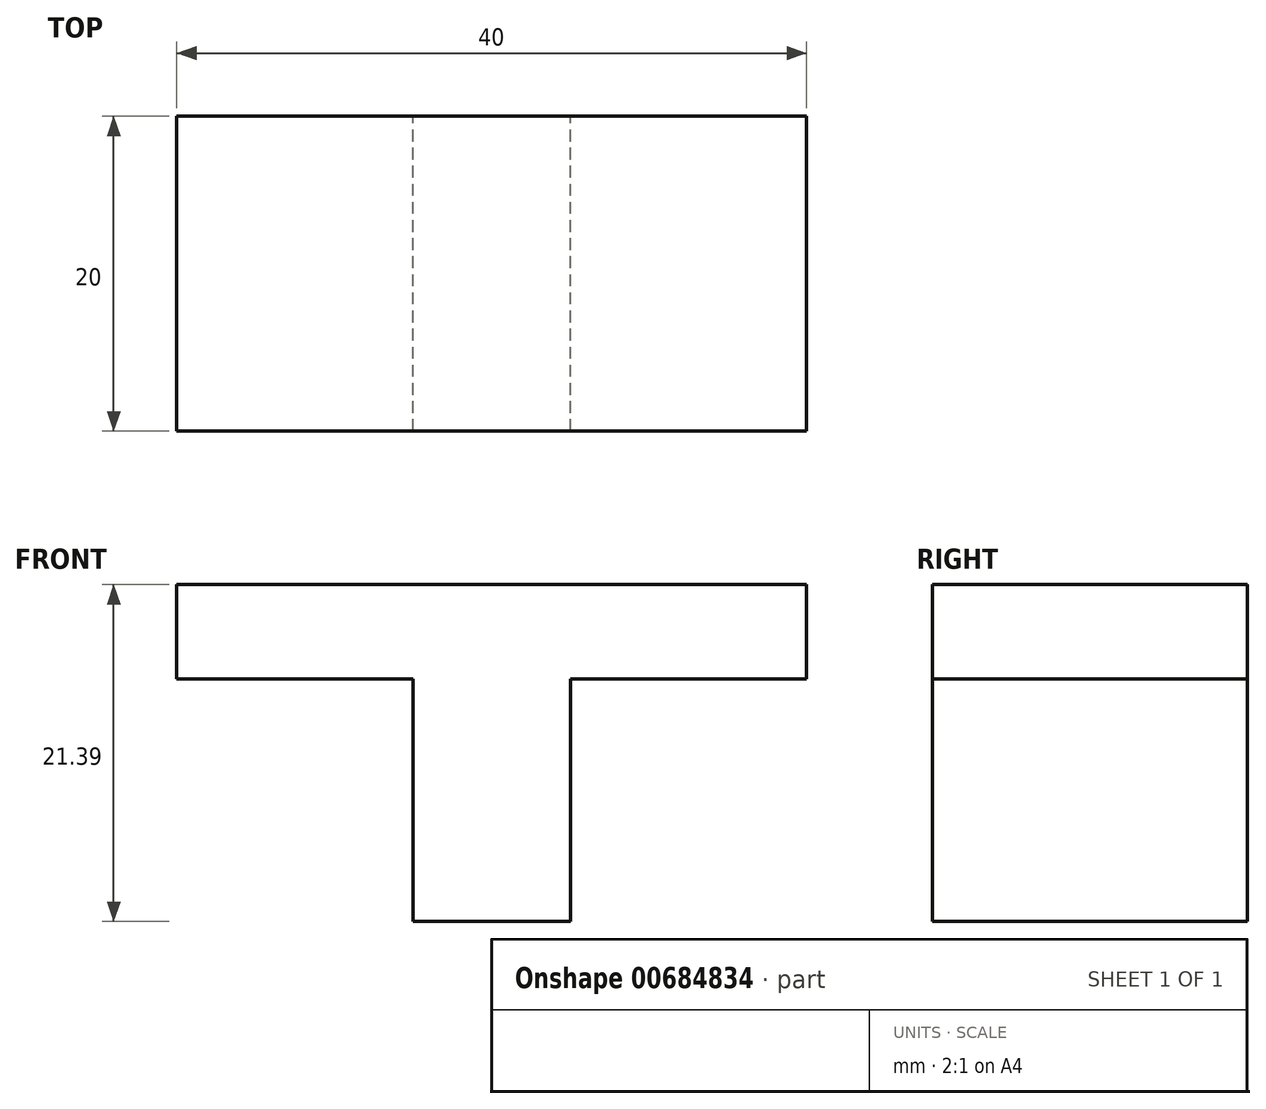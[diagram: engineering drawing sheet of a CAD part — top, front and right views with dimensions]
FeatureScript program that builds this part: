
annotation { "Feature Type Name" : "Feature", "Feature Type Description" : "" }
export const myFeature = defineFeature(function(context is Context, id is Id, definition is map)
    precondition{}
    {
        {
            var Q0;
            Q0=qCreatedBy(makeId("Front.planeOp"),FACE);
            var sketch = newSketch(context, id + "F0", { "sketchPlane" : qUnion([Q0])});
            skLineSegment(sketch, "E0", {"start": v(0, 0) * mm, "end": v(0, 21.4) * mm});
            skLineSegment(sketch, "E1", {"start": v(0, 21.4) * mm, "end": v(-20, 21.4) * mm});
            skLineSegment(sketch, "E2", {"start": v(-20, 21.4) * mm, "end": v(-20, 15.4) * mm});
            skLineSegment(sketch, "E3", {"start": v(-20, 15.4) * mm, "end": v(-5, 15.4) * mm});
            skLineSegment(sketch, "E4", {"start": v(-5, 15.4) * mm, "end": v(-5, 0) * mm});
            skLineSegment(sketch, "E5", {"start": v(-5, 0) * mm, "end": v(0, 0) * mm});
            skLineSegment(sketch, "E6.MirrorCS", {"start": v(5, 0) * mm, "end": v(0, 0) * mm});
            skLineSegment(sketch, "E7.MirrorCS", {"start": v(5, 15.4) * mm, "end": v(5, 0) * mm});
            skLineSegment(sketch, "E8.MirrorCS", {"start": v(20, 15.4) * mm, "end": v(5, 15.4) * mm});
            skLineSegment(sketch, "E9.MirrorCS", {"start": v(20, 21.4) * mm, "end": v(20, 15.4) * mm});
            skLineSegment(sketch, "E10.MirrorCS", {"start": v(0, 21.4) * mm, "end": v(20, 21.4) * mm});
            skSolve(sketch);
        }
        {
            var Q0;
            Q0 = qSketchRegion(id + "F0", true);
            extrude(context, id + "F1", {"entities" : qUnion([Q0]), "depth" : 20 * mm, "offsetDistance" : 25.4 * mm});
        }
    });
